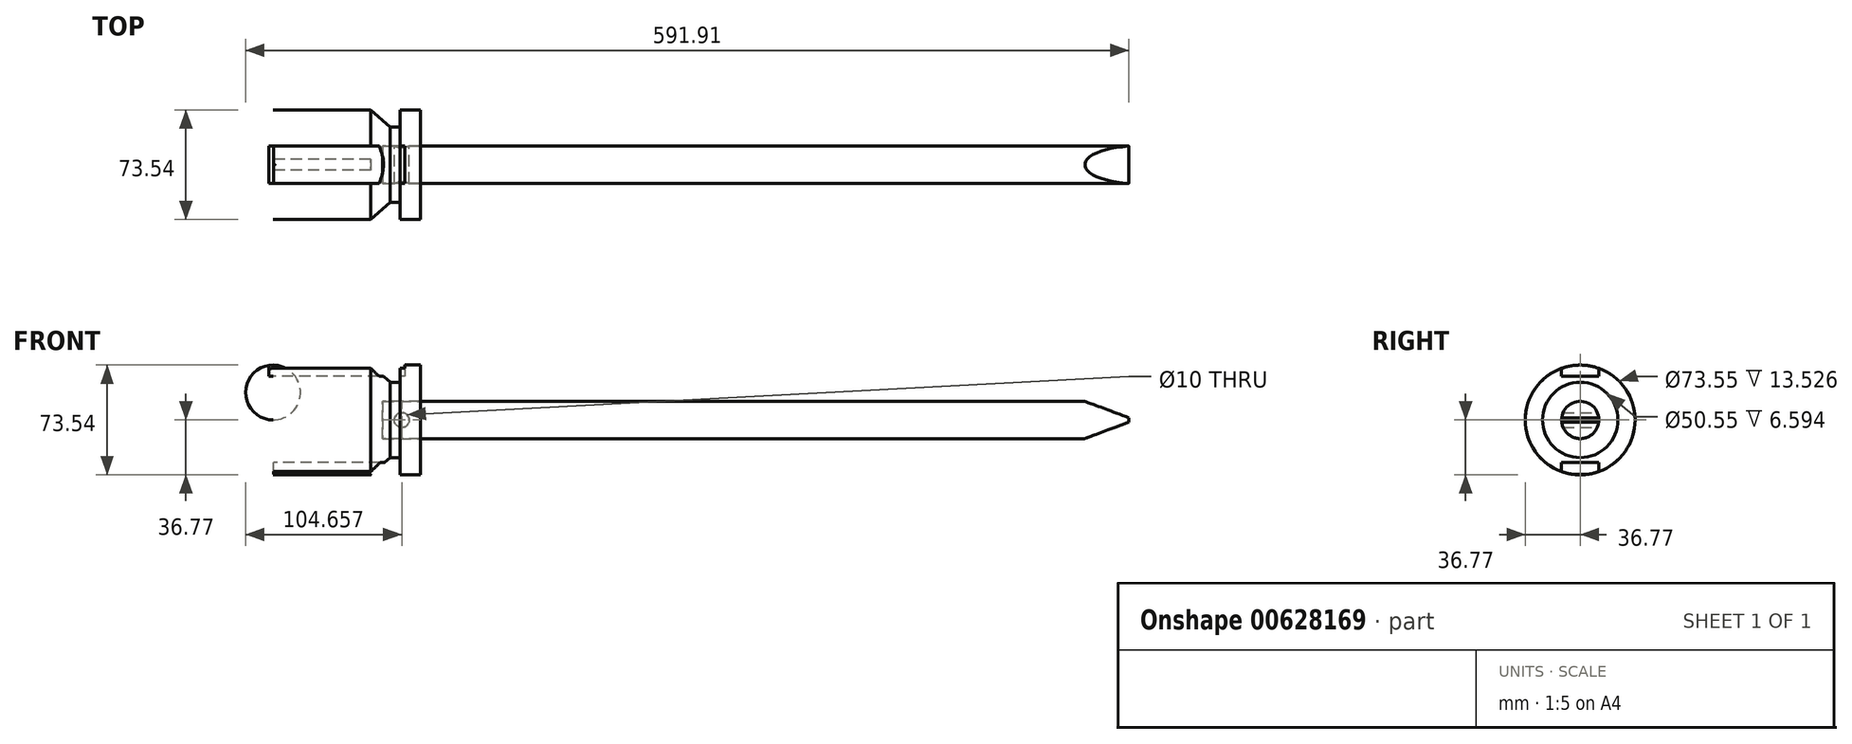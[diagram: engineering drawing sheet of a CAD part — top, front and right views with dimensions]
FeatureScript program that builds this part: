
annotation { "Feature Type Name" : "Feature", "Feature Type Description" : "" }
export const myFeature = defineFeature(function(context is Context, id is Id, definition is map)
    precondition{}
    {
        {
            var Q0;
            Q0=qCreatedBy(makeId("Right.planeOp"),FACE);
            var sketch = newSketch(context, id + "F0", { "sketchPlane" : qUnion([Q0])});
            skCircle(sketch, "E0", {"center": v(0, 0) * mm, "radius": 12.5 * mm});
            skSolve(sketch);
        }
        {
            var Q0;
            Q0=makeQuery(id+"F0.imprint","IMPRINT",FACE,{"disambiguationData":[TD([[makeQuery(id+"F0.imprint","IMPRINT",EDGE,{"derivedFrom":sQuery(id+"F0.wireOp",EDGE,"E0")}),1.0]])]});
            extrude(context, id + "F1", {"entities" : qUnion([Q0]), "oppositeDirection" : true, "depth" : 500 * mm, "offsetDistance" : 25 * mm});
        }
        {
            var Q0;
            Q0=qCreatedBy(makeId("Front.planeOp"),FACE);
            var sketch = newSketch(context, id + "F2", { "sketchPlane" : qUnion([Q0])});
            skCircle(sketch, "E1", {"center": v(-484.6, 0) * mm, "radius": 5 * mm});
            skLineSegment(sketch, "E2", {"start": v(0, 19.5) * mm, "end": v(-30, 19.5) * mm});
            skLineSegment(sketch, "E3", {"start": v(-30, 19.5) * mm, "end": v(-30, 12.64) * mm});
            skLineSegment(sketch, "E4", {"start": v(-30, 12.64) * mm, "end": v(0, 1.5) * mm});
            skLineSegment(sketch, "E5", {"start": v(0, 1.5) * mm, "end": v(0, 19.5) * mm});
            skLineSegment(sketch, "E6", {"start": v(0, 0) * mm, "end": v(0, 1.5) * mm});
            skLineSegment(sketch, "E7", {"start": v(0, 0) * mm, "end": v(0, -1.5) * mm});
            skLineSegment(sketch, "E8", {"start": v(0, -1.5) * mm, "end": v(0, -19.5) * mm});
            skLineSegment(sketch, "E9", {"start": v(-30, -19.5) * mm, "end": v(-30, -12.64) * mm});
            skLineSegment(sketch, "E10", {"start": v(-30, -12.64) * mm, "end": v(0, -1.5) * mm});
            skLineSegment(sketch, "E11", {"start": v(-30, -19.5) * mm, "end": v(0, -19.5) * mm});
            skSolve(sketch);
        }
        {
            var Q0;
            Q0=makeQuery(id+"F2.imprint","IMPRINT",FACE,{"disambiguationData":[TD([[makeQuery(id+"F2.imprint","IMPRINT",EDGE,{"derivedFrom":sQuery(id+"F2.wireOp",EDGE,"E2")}),1.0]])]});
            var Q1;
            Q1=makeQuery(id+"F2.imprint","IMPRINT",FACE,{"disambiguationData":[TD([[makeQuery(id+"F2.imprint","IMPRINT",EDGE,{"derivedFrom":sQuery(id+"F2.wireOp",EDGE,"E8")}),-1.0]])]});
            extrude(context, id + "F3", {"entities" : qUnion([Q0, Q1]), "operationType" : NewBodyOperationType.REMOVE, "endBound" : BoundingType.SYMMETRIC, "oppositeDirection" : true, "depth" : 25 * mm, "offsetDistance" : 25 * mm});
        }
        {
            var Q0;
            Q0=qCreatedBy(makeId("Front.planeOp"),FACE);
            var sketch = newSketch(context, id + "F4", { "sketchPlane" : qUnion([Q0])});
            skCircle(sketch, "E12", {"center": v(-487.25, 0) * mm, "radius": 5 * mm});
            skSolve(sketch);
        }
        {
            var Q0;
            Q0=qSketchRegion(id+"F4",true);
            extrude(context, id + "F5", {"entities" : qUnion([Q0]), "operationType" : NewBodyOperationType.REMOVE, "endBound" : BoundingType.SYMMETRIC, "depth" : 25 * mm, "offsetDistance" : 25 * mm});
        }
        {
            var Q0;
            Q0=qCreatedBy(makeId("Front.planeOp"),FACE);
            var sketch = newSketch(context, id + "F6", { "sketchPlane" : qUnion([Q0])});
            skLineSegment(sketch, "E13", {"start": v(-474.78, 12.6) * mm, "end": v(-499.97, 12.6) * mm});
            skLineSegment(sketch, "E14", {"start": v(-499.97, 12.6) * mm, "end": v(-499.97, 0) * mm});
            skLineSegment(sketch, "E15", {"start": v(-499.97, 0) * mm, "end": v(-573.52, 0) * mm});
            skArc(sketch, "E16", {"start": v(-573.52, 36.77) * mm, "mid": v(-591.9, 18.39) * mm, "end": v(-573.52, 0) * mm});
            skLineSegment(sketch, "E17", {"start": v(-573.52, 36.77) * mm, "end": v(-508.09, 36.77) * mm});
            skLineSegment(sketch, "E18", {"start": v(-508.09, 36.77) * mm, "end": v(-494.9, 25.28) * mm});
            skLineSegment(sketch, "E19", {"start": v(-494.9, 25.28) * mm, "end": v(-488.3, 25.28) * mm});
            skLineSegment(sketch, "E20", {"start": v(-488.3, 25.28) * mm, "end": v(-488.3, 36.77) * mm});
            skLineSegment(sketch, "E21", {"start": v(-474.78, 12.6) * mm, "end": v(-474.78, 36.77) * mm});
            skLineSegment(sketch, "E22", {"start": v(-474.78, 36.77) * mm, "end": v(-488.3, 36.77) * mm});
            skSolve(sketch);
        }
        {
            var Q0;
            Q0=makeQuery(id+"F6.imprint","IMPRINT",FACE,{"disambiguationData":[TD([[makeQuery(id+"F6.imprint","IMPRINT",EDGE,{"derivedFrom":sQuery(id+"F6.wireOp",EDGE,"E13")}),-1.0]])]});
            var Q1;
            Q1=makeQuery(id+"F1.opExtrude","SWEPT_FACE",FACE,{"disambiguationData":[OSD([sQuery(id+"F0.wireOp",EDGE,"E0")])]});
            revolve(context, id + "F7", {"entities" : qUnion([Q0]), "axis" : qUnion([Q1]), "revolveType" : RevolveType.FULL});
        }
        {
            var Q0;
            Q0=qCreatedBy(makeId("Front.planeOp"),FACE);
            var sketch = newSketch(context, id + "F8", { "sketchPlane" : qUnion([Q0])});
            skLineSegment(sketch, "E23.bottom", {"start": v(-485.14, 37.35) * mm, "end": v(-576.27, 37.35) * mm});
            skLineSegment(sketch, "E23.top", {"start": v(-485.14, 29.35) * mm, "end": v(-576.27, 29.35) * mm});
            skLineSegment(sketch, "E23.left", {"start": v(-485.14, 37.35) * mm, "end": v(-485.14, 29.35) * mm});
            skLineSegment(sketch, "E23.right", {"start": v(-576.27, 37.35) * mm, "end": v(-576.27, 29.35) * mm});
            skLineSegment(sketch, "E24.bottom", {"start": v(-488.3, -36.58) * mm, "end": v(-573.27, -36.58) * mm});
            skLineSegment(sketch, "E24.top", {"start": v(-488.3, -28.58) * mm, "end": v(-573.27, -28.58) * mm});
            skLineSegment(sketch, "E24.left", {"start": v(-488.3, -36.58) * mm, "end": v(-488.3, -28.58) * mm});
            skLineSegment(sketch, "E24.right", {"start": v(-573.27, -36.58) * mm, "end": v(-573.27, -28.58) * mm});
            skSolve(sketch);
        }
        {
            var Q0;
            Q0=makeQuery(id+"F8.imprint","IMPRINT",FACE,{"disambiguationData":[TD([[makeQuery(id+"F8.imprint","IMPRINT",EDGE,{"derivedFrom":sQuery(id+"F8.wireOp",EDGE,"E23.bottom")}),1.0]])]});
            var Q1;
            Q1=makeQuery(id+"F8.imprint","IMPRINT",FACE,{"disambiguationData":[TD([[makeQuery(id+"F8.imprint","IMPRINT",EDGE,{"derivedFrom":sQuery(id+"F8.wireOp",EDGE,"E24.bottom")}),-1.0]])]});
            extrude(context, id + "F9", {"entities" : qUnion([Q0, Q1]), "operationType" : NewBodyOperationType.REMOVE, "endBound" : BoundingType.SYMMETRIC, "depth" : 25 * mm, "offsetDistance" : 25 * mm});
        }
    });
